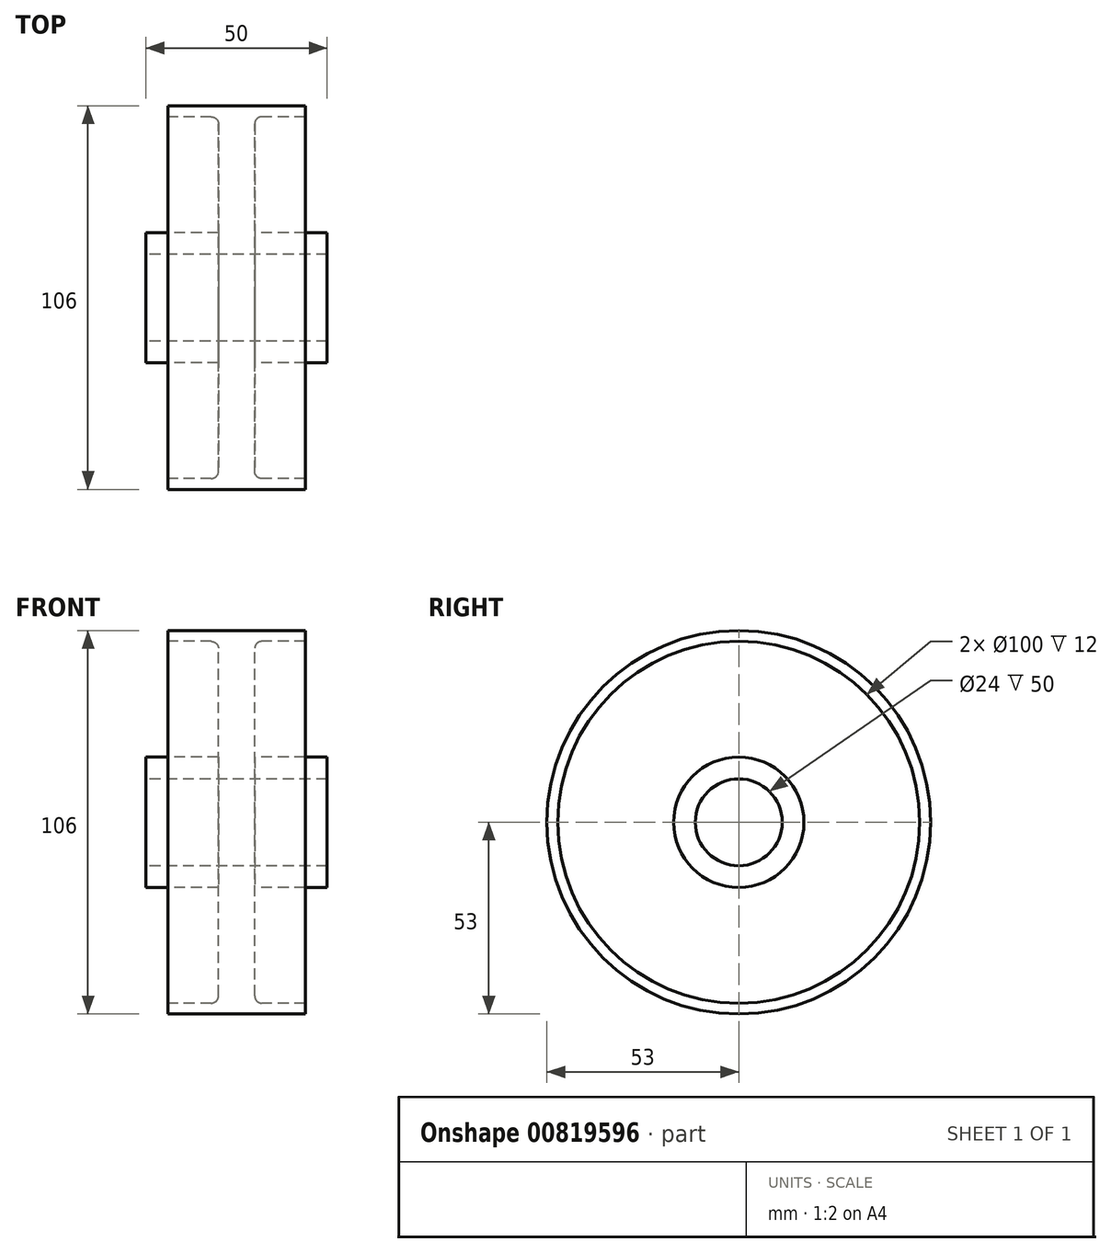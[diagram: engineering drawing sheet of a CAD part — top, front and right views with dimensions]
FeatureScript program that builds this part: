
annotation { "Feature Type Name" : "Feature", "Feature Type Description" : "" }
export const myFeature = defineFeature(function(context is Context, id is Id, definition is map)
    precondition{}
    {
        {
            var Q0;
            Q0=qCreatedBy(makeId("Front.planeOp"),FACE);
            var sketch = newSketch(context, id + "F0", { "sketchPlane" : qUnion([Q0])});
            skLineSegment(sketch, "E0", {"start": v(0, 0) * mm, "end": v(38, 0) * mm});
            skLineSegment(sketch, "E1", {"start": v(38, 0) * mm, "end": v(38, -3) * mm});
            skLineSegment(sketch, "E2", {"start": v(38, -3) * mm, "end": v(24, -3) * mm});
            skLineSegment(sketch, "E3", {"start": v(0, -3) * mm, "end": v(0, 0) * mm});
            skLineSegment(sketch, "E4", {"start": v(24, -3) * mm, "end": v(24, -35) * mm});
            skLineSegment(sketch, "E5.trimOffspring", {"start": v(12.18, -3) * mm, "end": v(0, -3) * mm});
            skPoint(sketch, "E6.orphan", {"position": v(19, -3) * mm});
            skLineSegment(sketch, "E7", {"start": v(12.18, -3) * mm, "end": v(14, -3) * mm});
            skLineSegment(sketch, "E8", {"start": v(14, -3) * mm, "end": v(14, -35) * mm});
            skLineSegment(sketch, "E9", {"start": v(24, -35) * mm, "end": v(44, -35) * mm});
            skLineSegment(sketch, "E10", {"start": v(44, -35) * mm, "end": v(44, -41) * mm});
            skLineSegment(sketch, "E11", {"start": v(44, -41) * mm, "end": v(-6, -41) * mm});
            skLineSegment(sketch, "E12", {"start": v(-6, -41) * mm, "end": v(-6, -35) * mm});
            skLineSegment(sketch, "E13", {"start": v(-6, -35) * mm, "end": v(14, -35) * mm});
            skLineSegment(sketch, "E14", {"start": v(-36.34, -53) * mm, "end": v(70.32, -53) * mm});
            skSolve(sketch);
        }
        {
            var Q0;
            Q0=makeQuery(id+"F0.imprint","IMPRINT",FACE,{"disambiguationData":[TD([[makeQuery(id+"F0.imprint","IMPRINT",EDGE,{"derivedFrom":sQuery(id+"F0.wireOp",EDGE,"E0")}),-1.0]])]});
            var Q1;
            Q1=sQuery(id+"F0.wireOp",EDGE,"E14");
            revolve(context, id + "F1", {"surfaceOperationType" : NewSurfaceOperationType.NEW, "entities" : qUnion([Q0]), "axis" : qUnion([Q1]), "revolveType" : RevolveType.FULL});
        }
        {
            var Q0;
            Q0=makeQuery(id+"F1.opRevolve","SWEPT_EDGE",EDGE,{"disambiguationData":[OSD([sQuery(id+"F0.wireOp",EDGE,"E7"),sQuery(id+"F0.wireOp",EDGE,"E8")])]});
            var Q1;
            Q1=makeQuery(id+"F1.opRevolve","SWEPT_EDGE",EDGE,{"disambiguationData":[OSD([sQuery(id+"F0.wireOp",EDGE,"E2"),sQuery(id+"F0.wireOp",EDGE,"E4")])]});
            fillet(context, id + "F2", {"entities" : qUnion([Q0, Q1]), "radius" : 2 * mm, "tangentPropagation" : true, "allowEdgeOverflow" : false});
        }
    });
